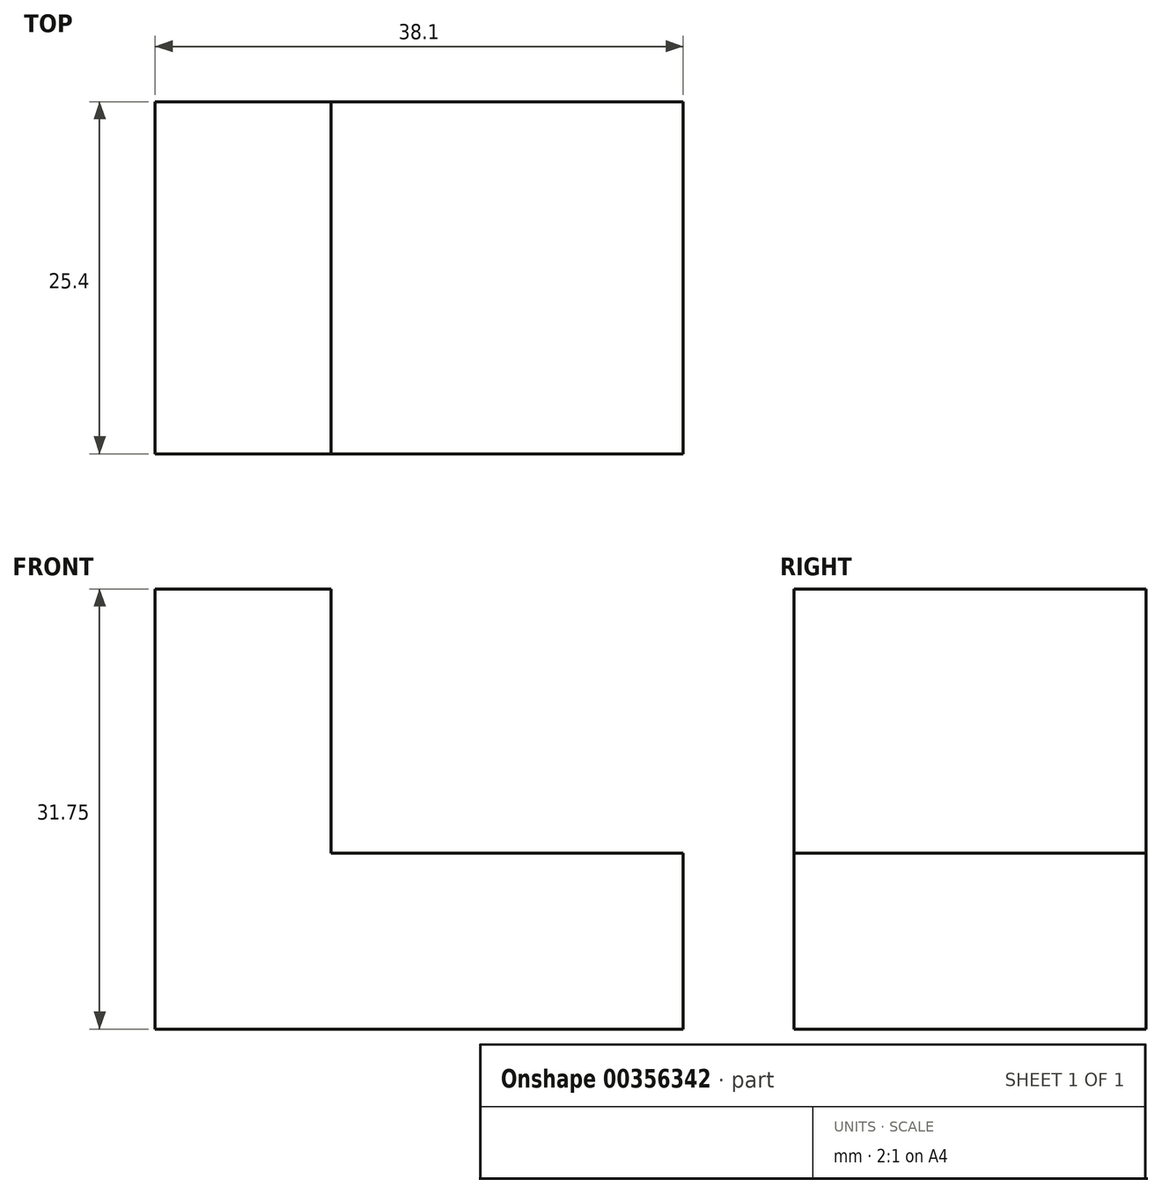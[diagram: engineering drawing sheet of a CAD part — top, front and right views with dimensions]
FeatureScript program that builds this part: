
annotation { "Feature Type Name" : "Feature", "Feature Type Description" : "" }
export const myFeature = defineFeature(function(context is Context, id is Id, definition is map)
    precondition{}
    {
        {
            var Q0;
            Q0=qCreatedBy(makeId("Front.planeOp"),FACE);
            var sketch = newSketch(context, id + "F0", { "sketchPlane" : qUnion([Q0])});
            skLineSegment(sketch, "E0", {"start": v(0, 31.75) * mm, "end": v(0, 0) * mm});
            skLineSegment(sketch, "E1", {"start": v(0, 0) * mm, "end": v(38.1, 0) * mm});
            skLineSegment(sketch, "E2", {"start": v(38.1, 0) * mm, "end": v(38.1, 12.7) * mm});
            skLineSegment(sketch, "E3", {"start": v(38.1, 12.7) * mm, "end": v(12.7, 12.7) * mm});
            skLineSegment(sketch, "E4", {"start": v(12.7, 12.7) * mm, "end": v(12.7, 31.75) * mm});
            skLineSegment(sketch, "E5", {"start": v(12.7, 31.75) * mm, "end": v(0, 31.75) * mm});
            skSolve(sketch);
        }
        {
            var Q0;
            Q0=makeQuery(id+"F0.imprint","IMPRINT",FACE,{"disambiguationData":[TD([[makeQuery(id+"F0.imprint","IMPRINT",EDGE,{"derivedFrom":sQuery(id+"F0.wireOp",EDGE,"E0")}),1.0]])]});
            extrude(context, id + "F1", {"entities" : qUnion([Q0]), "depth" : 25.4 * mm});
        }
    });
